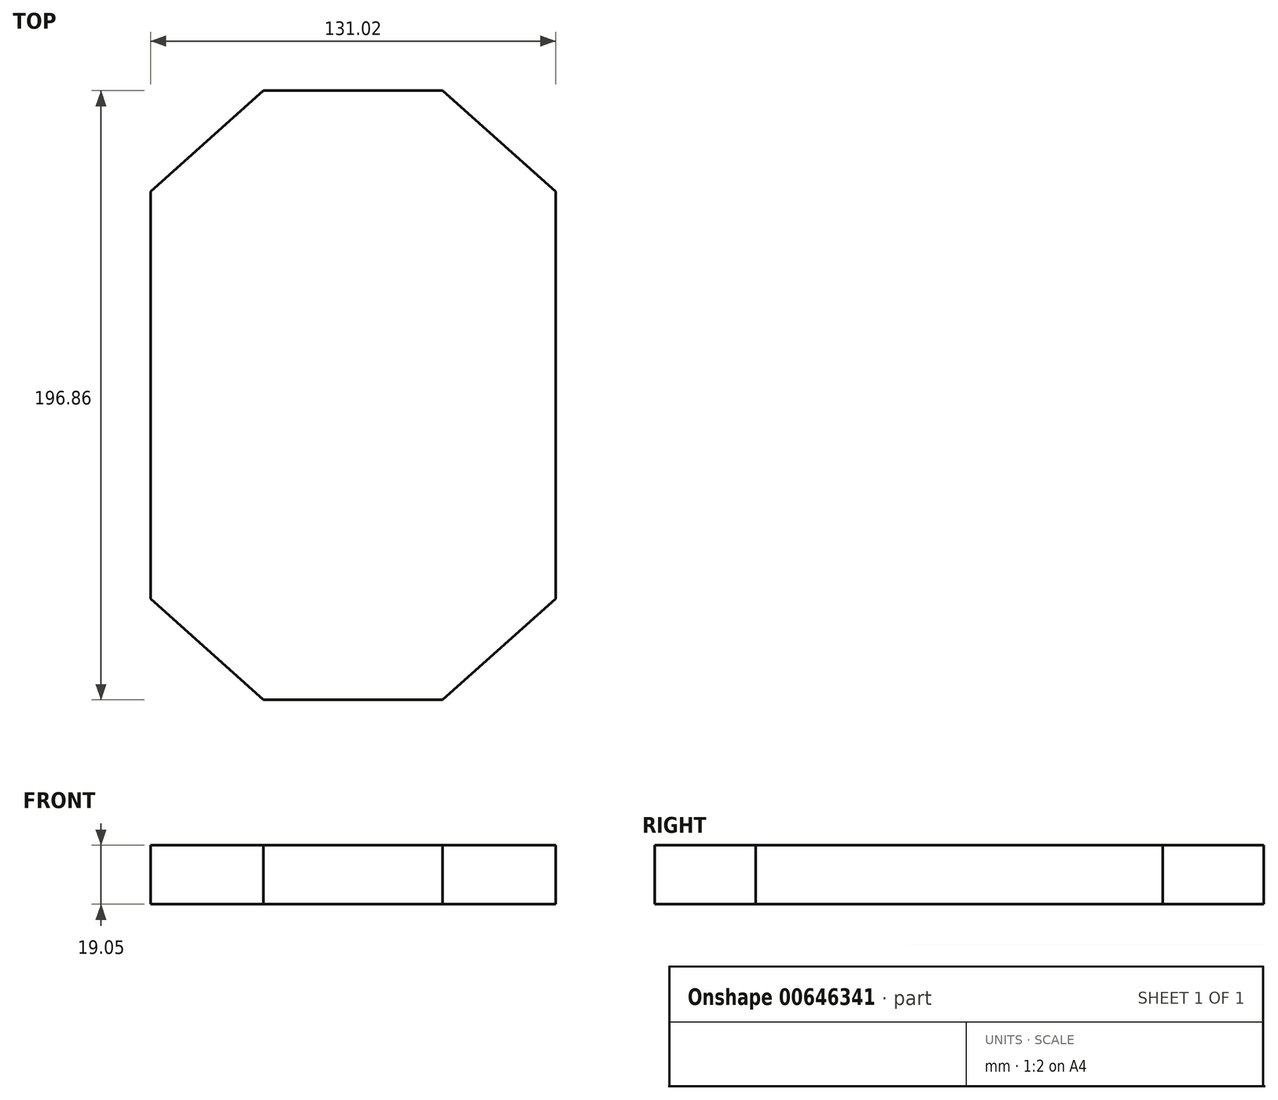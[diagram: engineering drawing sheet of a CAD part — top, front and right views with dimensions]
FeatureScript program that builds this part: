
annotation { "Feature Type Name" : "Feature", "Feature Type Description" : "" }
export const myFeature = defineFeature(function(context is Context, id is Id, definition is map)
    precondition{}
    {
        {
            var Q0;
            Q0=qCreatedBy(makeId("Top.planeOp"),FACE);
            var sketch = newSketch(context, id + "F0", { "sketchPlane" : qUnion([Q0])});
            skLineSegment(sketch, "E0.bottom", {"start": v(28.96, 98.43) * mm, "end": v(-28.96, 98.43) * mm});
            skLineSegment(sketch, "E0.top", {"start": v(28.96, -98.43) * mm, "end": v(-28.96, -98.43) * mm});
            skLineSegment(sketch, "E0.left", {"start": v(28.96, 98.43) * mm, "end": v(28.96, -98.43) * mm});
            skLineSegment(sketch, "E0.right", {"start": v(-28.96, 98.43) * mm, "end": v(-28.96, -98.43) * mm});
            skPoint(sketch, "E0.middle", {"position": v(0, 0) * mm});
            skLineSegment(sketch, "E1.bottom", {"start": v(-65.51, 65.79) * mm, "end": v(65.51, 65.79) * mm});
            skLineSegment(sketch, "E1.top", {"start": v(-65.51, -65.79) * mm, "end": v(65.51, -65.79) * mm});
            skLineSegment(sketch, "E1.left", {"start": v(-65.51, 65.79) * mm, "end": v(-65.51, -65.79) * mm});
            skLineSegment(sketch, "E1.right", {"start": v(65.51, 65.79) * mm, "end": v(65.51, -65.79) * mm});
            skLineSegment(sketch, "E2", {"start": v(-28.96, -98.43) * mm, "end": v(-65.51, -65.79) * mm});
            skLineSegment(sketch, "E3", {"start": v(28.96, -98.43) * mm, "end": v(65.51, -65.79) * mm});
            skLineSegment(sketch, "E4", {"start": v(65.51, 65.79) * mm, "end": v(28.96, 98.43) * mm});
            skLineSegment(sketch, "E5", {"start": v(-65.51, 65.79) * mm, "end": v(-28.96, 98.43) * mm});
            skSolve(sketch);
        }
        {
            var Q0;
            {var subQ0=sQuery(id+"F0.wireOp",EDGE,"E0.bottom");Q0=makeQuery(id+"F0.imprint","IMPRINT",FACE,{"disambiguationData":[TD([[makeQuery(id+"F0.imprint","IMPRINT",EDGE,{"derivedFrom":subQ0}),1.0]])]});}
            var Q1;
            {var subQ5=sQuery(id+"F0.wireOp",EDGE,"E1.left");Q1=makeQuery(id+"F0.imprint","IMPRINT",FACE,{"disambiguationData":[TD([[makeQuery(id+"F0.imprint","IMPRINT",EDGE,{"derivedFrom":subQ5}),1.0]])]});}
            var Q2;
            {var subQ0=sQuery(id+"F0.wireOp",EDGE,"E5");Q2=makeQuery(id+"F0.imprint","IMPRINT",FACE,{"disambiguationData":[TD([[makeQuery(id+"F0.imprint","IMPRINT",EDGE,{"derivedFrom":subQ0}),-1.0]])]});}
            var Q3;
            {var subQ0=sQuery(id+"F0.wireOp",EDGE,"E1.bottom");var subQ1=sQuery(id+"F0.wireOp",EDGE,"E0.left");var subQ2=makeQuery(id+"F0.imprint","INTERSECT",VERTEX,{"derivedFrom":[subQ1,subQ0]});Q3=makeQuery(id+"F0.imprint","IMPRINT",FACE,{"disambiguationData":[TD([[makeQuery(id+"F0.imprint","IMPRINT",EDGE,{"disambiguationData":[TD([[subQ2,-1.0]])],"derivedFrom":subQ1}),-1.0]])]});}
            var Q4;
            {var subQ5=sQuery(id+"F0.wireOp",EDGE,"E1.right");Q4=makeQuery(id+"F0.imprint","IMPRINT",FACE,{"disambiguationData":[TD([[makeQuery(id+"F0.imprint","IMPRINT",EDGE,{"derivedFrom":subQ5}),-1.0]])]});}
            var Q5;
            {var subQ0=sQuery(id+"F0.wireOp",EDGE,"E4");Q5=makeQuery(id+"F0.imprint","IMPRINT",FACE,{"disambiguationData":[TD([[makeQuery(id+"F0.imprint","IMPRINT",EDGE,{"derivedFrom":subQ0}),1.0]])]});}
            var Q6;
            {var subQ0=sQuery(id+"F0.wireOp",EDGE,"E3");Q6=makeQuery(id+"F0.imprint","IMPRINT",FACE,{"disambiguationData":[TD([[makeQuery(id+"F0.imprint","IMPRINT",EDGE,{"derivedFrom":subQ0}),1.0]])]});}
            var Q7;
            {var subQ0=sQuery(id+"F0.wireOp",EDGE,"E0.top");Q7=makeQuery(id+"F0.imprint","IMPRINT",FACE,{"disambiguationData":[TD([[makeQuery(id+"F0.imprint","IMPRINT",EDGE,{"derivedFrom":subQ0}),-1.0]])]});}
            var Q8;
            {var subQ0=sQuery(id+"F0.wireOp",EDGE,"E2");Q8=makeQuery(id+"F0.imprint","IMPRINT",FACE,{"disambiguationData":[TD([[makeQuery(id+"F0.imprint","IMPRINT",EDGE,{"derivedFrom":subQ0}),-1.0]])]});}
            extrude(context, id + "F1", {"entities" : qUnion([Q0, Q1, Q2, Q3, Q4, Q5, Q6, Q7, Q8]), "depth" : 19.05 * mm, "offsetDistance" : 25.4 * mm});
        }
    });
